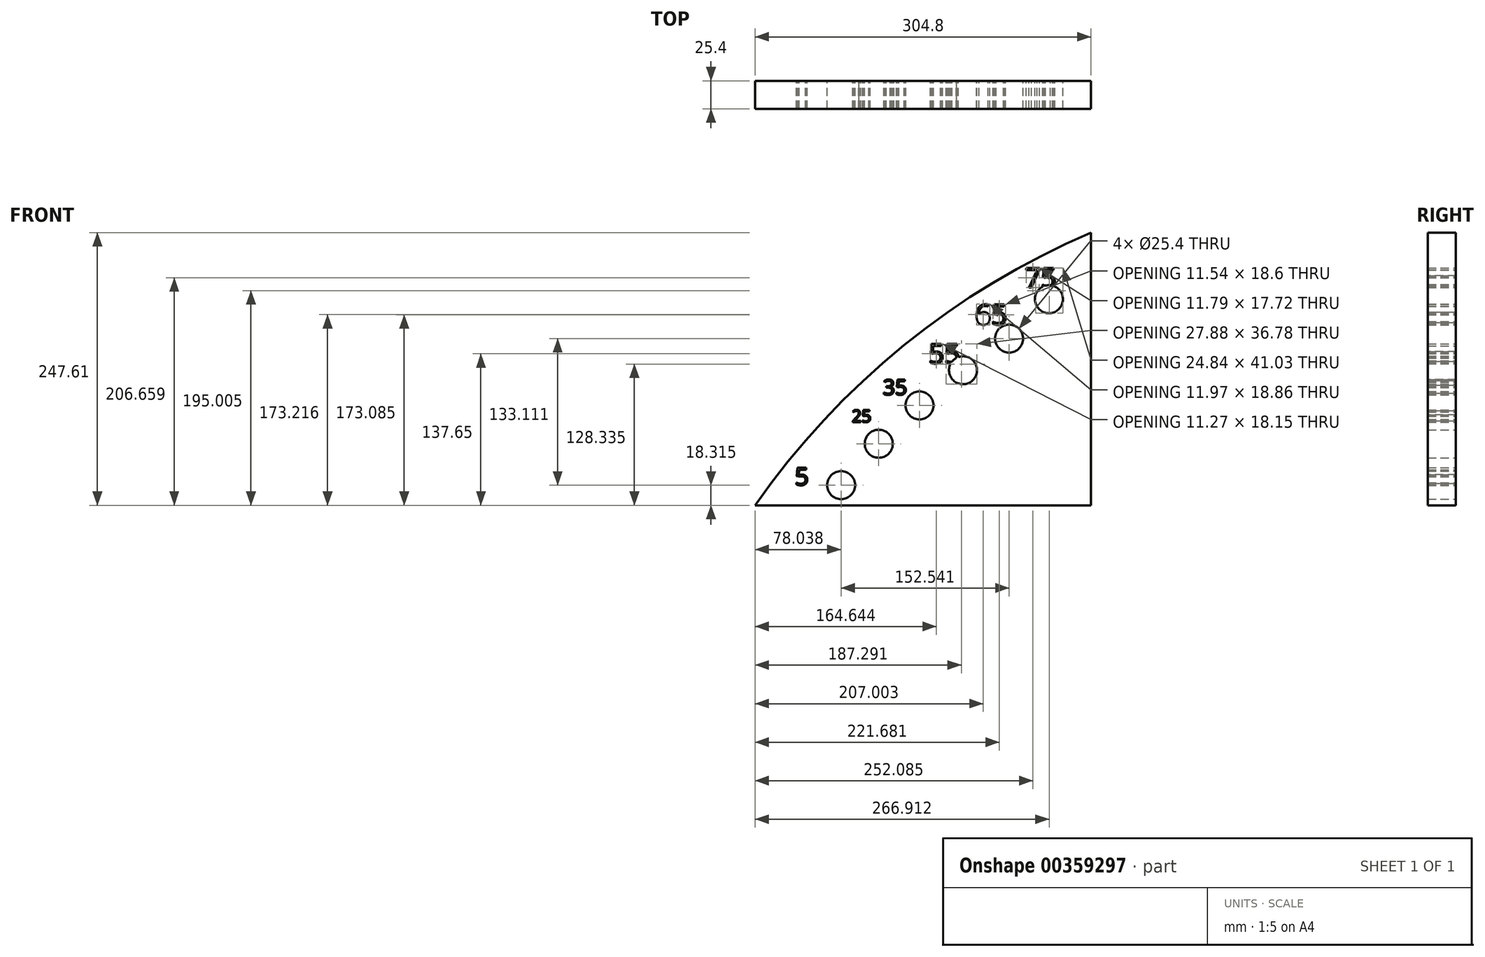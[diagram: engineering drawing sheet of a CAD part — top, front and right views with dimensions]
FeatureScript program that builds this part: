
annotation { "Feature Type Name" : "Feature", "Feature Type Description" : "" }
export const myFeature = defineFeature(function(context is Context, id is Id, definition is map)
    precondition{}
    {
        {
            var Q0;
            Q0=qCreatedBy(makeId("Front.planeOp"),FACE);
            var sketch = newSketch(context, id + "F0", { "sketchPlane" : qUnion([Q0])});
            skLineSegment(sketch, "E0", {"start": v(71.22, 31.94) * mm, "end": v(71.22, -222.14) * mm});
            skArc(sketch, "E1", {"start": v(71.22, 31.94) * mm, "mid": v(-98.56, -70.47) * mm, "end": v(-233.58, -215.67) * mm});
            skLineSegment(sketch, "E2", {"start": v(-233.58, -215.67) * mm, "end": v(71.22, -215.67) * mm});
            skCircle(sketch, "E3", {"center": v(-155.54, -197.36) * mm, "radius": 12.7 * mm});
            skCircle(sketch, "E4", {"center": v(-121.36, -159.78) * mm, "radius": 12.7 * mm});
            skCircle(sketch, "E5", {"center": v(-84.39, -124.94) * mm, "radius": 12.7 * mm});
            skCircle(sketch, "E6", {"center": v(-44.86, -93.03) * mm, "radius": 12.7 * mm});
            skCircle(sketch, "E7", {"center": v(-3, -64.24) * mm, "radius": 12.7 * mm});
            skCircle(sketch, "E8", {"center": v(33.12, -28.53) * mm, "radius": 12.7 * mm});
            skText(sketch, "E9", { "text": "5\n", "fontName": "OpenSans-Regular.ttf"});
            skText(sketch, "E10", { "text": "25", "fontName": "OpenSans-Regular.ttf"});
            skText(sketch, "E11", { "text": "35", "fontName": "OpenSans-Regular.ttf"});
            skText(sketch, "E12", { "text": "55", "fontName": "OpenSans-Regular.ttf"});
            skText(sketch, "E13", { "text": "65\n", "fontName": "OpenSans-Regular.ttf"});
            skText(sketch, "E14", { "text": "75\n", "fontName": "OpenSans-Regular.ttf"});
            const initialGuessF0  = {"E9": [-0.19747, -0.19736, 1, 0, 0.0159], "E10": [-0.14586, -0.14018, 1, 0, 0.01118], "E11": [-0.11748, -0.11524, 1, 0, 0.01376], "E12": [-0.0762, -0.08685, 1, 0, 0.01806], "E13": [-0.03403, -0.05163, 1, 0, 0.0185], "E14": [0.01147, -0.01787, 1, 0, 0.01787]};
            skSetInitialGuess(sketch, initialGuessF0);
            skSolve(sketch);
        }
        {
            var Q0;
            {var subQ13=sQuery(id+"F0.wireOp",EDGE,"E1");Q0=makeQuery(id+"F0.imprint","IMPRINT",FACE,{"disambiguationData":[TD([[makeQuery(id+"F0.imprint","IMPRINT",EDGE,{"derivedFrom":subQ13}),1.0]])]});}
            extrude(context, id + "F1", {"entities" : qUnion([Q0]), "depth" : 25.4 * mm});
        }
    });
